# Revit family: HL_Трап для внутренних помещений_HL510NPrG
name_source: partatom
category: Instalační zařizovací předměty
revit_build: Autodesk Revit 2016 (Build: 20151007_0715(x64)
units: mm (PartAtom-declared; Revit-internal decimal feet)

## family parameters
Bod výpočtu místnosti = Ano
Kóta kulaté spojky = Použít průměr
Nadpis OmniClass = Deck Waste Water Drains
Ořezat dutým tvarem při načtení = Ne
Sdílené = Ano
Typ součásti = Normální
Vždy vertikální = Ano
Založené na pracovní rovině = Ne
Číslo OmniClass = 23.70.50.21.24.14

## types (2) — shared parameters
EAN = 9003076004713
Klíčová poznámka = HL510NPrG
Komentáře k typům = HL510NPrG Трап для внутренних помещений DN40/50 горизонтальный с запахозапирающим устройством Primus, 150х150мм/137х137мм чугун
Model = HL510NPrG
Popis = Трапы для внутренних помещений
Připojení CW = Ne
Připojení HW = Ne
Připojení odpadu = Ano
Připojení ventilace = Ne
URL = http://www.hutterer-lechner.com
Výrobce = HL Hutterer & Lechner GmbH
ВЕС = 2,43 [kg]
ВЫСОТА МОНТАЖА = 114 mm
МАКСИМАЛЬНАЯ НАГРУЗКА КЛАССА = A/L15 - 1,5 t
МАТЕРИАЛ = PE
НАСАДКА = 35-75 mm / 150 x 150 mm / GJL
ПРОИЗВОДИТЕЛЬНОСТЬ = 0,50 l/s
ПРОПУСКНАЯ СПОСОБНОСТЬ = 0.5 L/s
РАЗМЕР = DN40/50
РЕШЁТКА = 137 x 137 mm / GJL

## type names (no varying parameters)
- 160_HL37N.1
- HL510NPrG

## geometry (parser evidence)
native form markers: Sweep x41
no freeform markers — native parametric forms only
